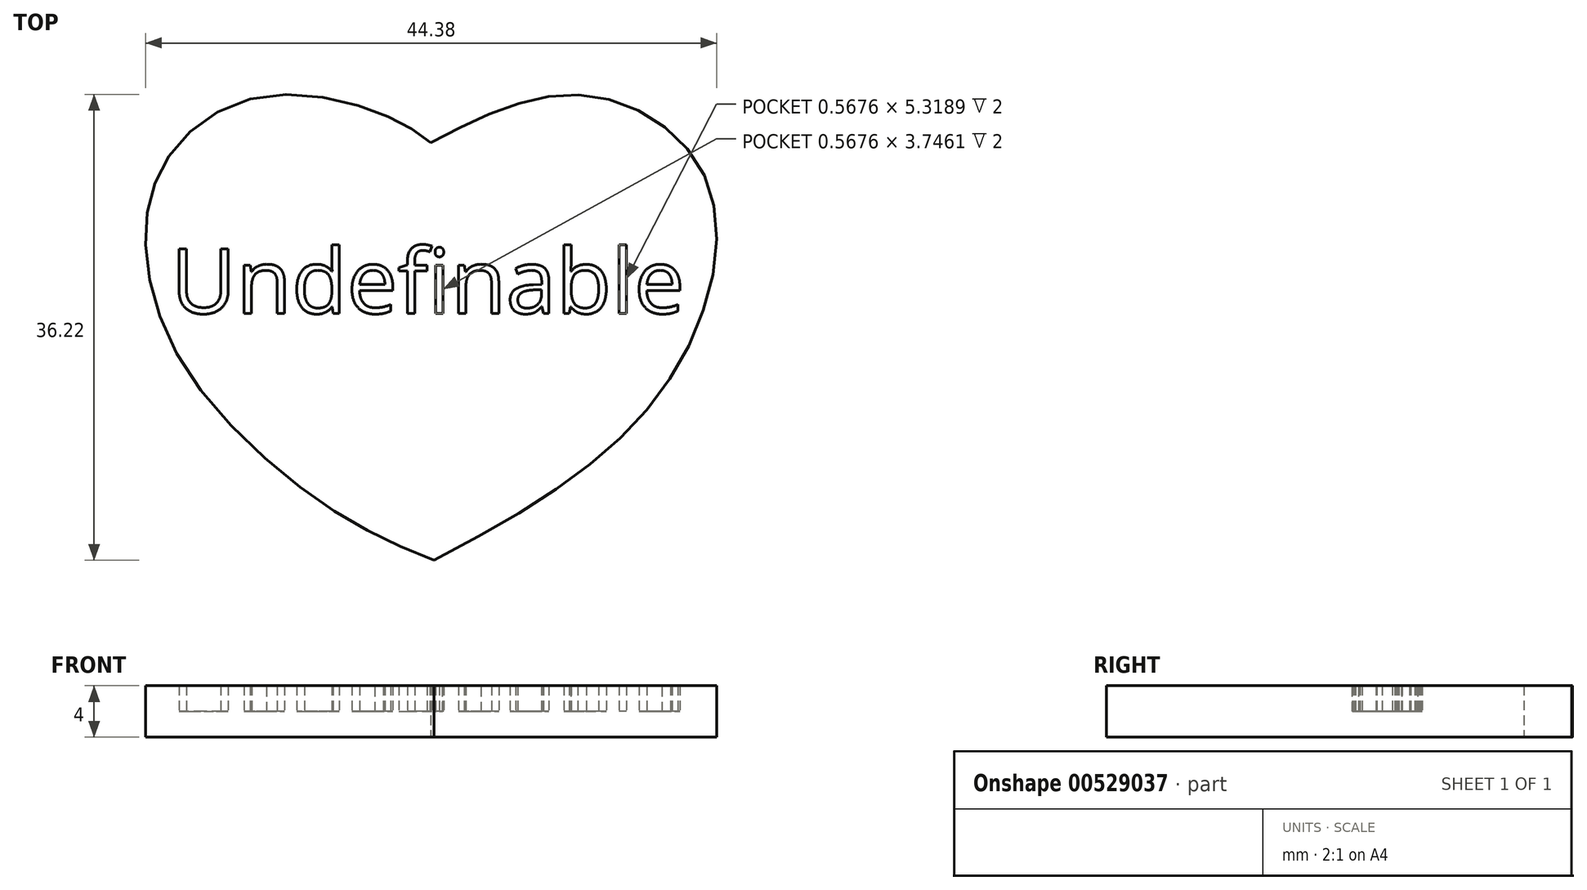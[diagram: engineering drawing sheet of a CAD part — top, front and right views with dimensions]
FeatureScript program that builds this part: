
annotation { "Feature Type Name" : "Feature", "Feature Type Description" : "" }
export const myFeature = defineFeature(function(context is Context, id is Id, definition is map)
    precondition{}
    {
        {
            var Q0;
            Q0=qCreatedBy(makeId("Top.planeOp"),FACE);
            var sketch = newSketch(context, id + "F0", { "sketchPlane" : qUnion([Q0])});
            skFitSpline(sketch, "E0", {"points": [v(49.6, 70.34) * mm, v(73.34, 77.72) * mm, v(92.4, 64.64) * mm, v(87.02, 34) * mm, v(50.07, 5.42) * mm], "startDerivative": vector(104.52, 55.2) * mm, "endDerivative": vector(-164.24, -85.38) * mm});
            skFitSpline(sketch, "E1", {"points": [v(49.6, 70.34) * mm, v(40.98, 75.22) * mm, v(22.79, 77.45) * mm, v(9.23, 68.72) * mm, v(5.28, 55.8) * mm, v(10.9, 36.23) * mm, v(31.88, 14.89) * mm, v(50.07, 5.42) * mm], "startDerivative": vector(-61.26, 53.1) * mm, "endDerivative": vector(123.7, -48.3) * mm});
            skSolve(sketch);
        }
        {
            var Q0;
            Q0=makeQuery(id+"F0.imprint","IMPRINT",FACE,{"disambiguationData":[TD([[makeQuery(id+"F0.imprint","IMPRINT",EDGE,{"derivedFrom":sQuery(id+"F0.wireOp",EDGE,"E0")}),-1.0]])]});
            extrude(context, id + "F1", {"entities" : qUnion([Q0]), "endBound" : BoundingType.SYMMETRIC, "depth" : 8 * mm, "offsetDistance" : 25 * mm});
        }
        {
            var Q0;
            Q0=makeQuery(id+"F1.opExtrude","SWEPT_BODY",BODY,{"disambiguationData":[OSD([sQuery(id+"F0.wireOp",EDGE,"E0"),sQuery(id+"F0.wireOp",EDGE,"E1")])]});
            var Q1;
            Q1=qCreatedBy(makeId("Origin.pointOp"),VERTEX);
            transform(context, id + "F2", {"entities" : qUnion([Q0]), "transformType" : TransformType.SCALE_UNIFORMLY, "scale" : .5, "scalePoint" : qUnion([Q1]), "makeCopy" : false});
        }
        {
            var Q0;
            Q0=qCreatedBy(makeId("Top.planeOp"),FACE);
            var sketch = newSketch(context, id + "F3", { "sketchPlane" : qUnion([Q0])});
            skText(sketch, "E2", { "text": "Undefinable", "fontName": "OpenSans-Regular.ttf"});
            const initialGuessF3  = {"E2": [0.0046, 0.02191, 1, 0, 0.00504]};
            skSetInitialGuess(sketch, initialGuessF3);
            skSolve(sketch);
        }
        {
            var Q0;
            Q0 = qSketchRegion(id + "F3", true);
            extrude(context, id + "F4", {"entities" : qUnion([Q0]), "operationType" : NewBodyOperationType.REMOVE, "depth" : 3 * mm, "offsetDistance" : 25 * mm});
        }
    });
